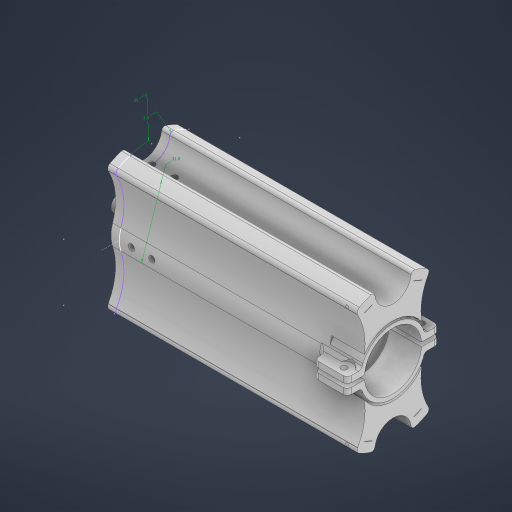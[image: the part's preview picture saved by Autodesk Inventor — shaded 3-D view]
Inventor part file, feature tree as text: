
AUTODESK INVENTOR PART (.ipt)
format: ipt  version: 2024.2 (Build 282272000, 272)  size: 1,191,424 bytes
history: native  units: in
note: dims shown in document units (in); Inventor stores cm internally (conversion verified against a paired STEP export)
features: extrude x20, sketch x18, mirror x7, projected_geometry x6, fillet x3, chamfer x1
ambient origin geometry x8: Origin, YZ Plane, XZ Plane, XY Plane, X Axis, Y Axis, Z Axis, Center Point
bodies: Solid1 (feature_tree)
feature tree (55):
  extrude  "Extrusion1"  Depth=0.0394in
  extrude  "Extrusion2"  Depth=0.0787in
  mirror  "Mirror1"
  fillet  "Fillet1"  Radius=0.0394in
  extrude  "Extrusion3"  Depth=0.1969in
  sketch  "Sketch4"  dims[d9=0.1181in d10=0.1378in d11=0.2756in]
  extrude  "Extrusion4"  Depth=0.1181in
  fillet  "Fillet2"  Radius=0.2756in
  extrude  "Extrusion5"  Depth=0.0787in
  sketch  "Sketch6"  dims[d15=0.3819in d16=0.1654in d17=0.0in]
  sketch  "Sketch7"  dims[d18=0.1181in d19=1.0945in]
  extrude  "Extrusion6"  Depth=0.1654in TaperAngle=0.0deg
  extrude  "Extrusion7"  Depth=0.1181in
  extrude  "Extrusion8"  Depth=0.0787in
  extrude  "Extrusion10"  Depth=0.1575in
  mirror  "Mirror4"
  mirror  "Mirror5"
  extrude  "Extrusion12"  Depth=0.0787in
  extrude  "Extrusion11"  Depth=2.7559in
  extrude  "Extrusion13"  Depth=0.3937in
  extrude  "Extrusion14"  Depth=1.9685in
  extrude  "Extrusion15"  Depth=0.0591in
  mirror  "Mirror6"
  mirror  "Mirror7"
  extrude  "Extrusion16"  Depth=4.6457in TaperAngle=0.0deg
  extrude  "Extrusion17"  Depth=0.3937in TaperAngle=0.0deg
  extrude  "Extrusion18"  Depth=1.3386in
  extrude  "Extrusion19"  Depth=0.0787in
  extrude  "Extrusion20"  Depth=0.0787in
  chamfer  "Chamfer1"  Distance=0.3937in
  fillet  "Fillet3"  [1 undecoded]
  extrude  "Extrusion9"  Depth=0.0787in
  mirror  "Mirror2"
  mirror  "Mirror3"
  sketch  "Sketch1"  dims[d0=1.0945in d1=0.0394in]
  sketch  "Sketch2"  dims[d3=0.1181in d4=0.0787in d5=0.0394in]
  sketch  "Sketch3"  dims[d6=0.6299in d7=0.0in d8=0.1969in]
  sketch  "Sketch5"  dims[d12=0.6299in d13=0.0in d14=0.0787in]
  sketch  "Sketch8"  dims[d20=0.0787in d21=1.252in]
  projected_geometry  "Projected Loop1"
  projected_geometry  "Projected Loop2"
  sketch  "Sketch10"  dims[d22=0.3937in d23=0.0in d24=0.1575in]
  sketch  "Sketch11"  dims[d25=0.1575in d26=0.0787in]
  projected_geometry  "Projected Loop3"
  sketch  "Sketch12"  dims[d27=3.4567in d28=0.0in d29=2.7559in]
  projected_geometry  "Projected Loop4"
  sketch  "Sketch13"  dims[d30=0.3937in d31=0.3937in]
  sketch  "Sketch14"  dims[d32=2.7559in d33=1.9685in]
  sketch  "Sketch15"  dims[d36=1.378in d40=0.0591in]
  sketch  "Sketch16"  dims[d41=1.252in d42=4.6457in d43=0.0in]
  sketch  "Sketch17"  dims[d44=2.7559in d45=0.3937in d46=0.0in]
  projected_geometry  "Projected Loop5"
  projected_geometry  "Projected Loop6"
  sketch  "Sketch18"  dims[d47=5.8121in d48=0.0in d49=1.3386in]
  sketch  "Sketch19"  dims[d50=0.0689in d51=0.0394in d52=1.9685in d54=0.0825in d56=0.3937in d57=0.0in d58=0.0in d59=0.0in d63=0.0079in d64=0.3091in d65=0.1181in d66=0.4724in d67=0.0in d68=0.1575in d69=0.0in d70=0.35in d71=0.0787in d72=0.0in d73=1.1024in d74=0.0787in d75=0.0in d76=0.315in d77=0.3937in d78=0.0in d79=1.2598in d80=1.3386in d81=0.3937in d82=0.0in d83=0.7874in d84=0.0in d85=0.3937in d86=0.1181in d87=0.0in d88=0.0in d89=0.3937in d90=0.0in d91=0.5906in d92=0.0in d93=0.0in d94=0.1181in d96=0.3937in d97=0.1181in d98=0.0787in d99=0.0787in d100=45.0deg d101=0.0787in]
note: 1 required parameter value undecoded (feature->parameter linkage not recoverable at this tier; creation-order binding heuristic only, values carry confidence <= 0.55)
